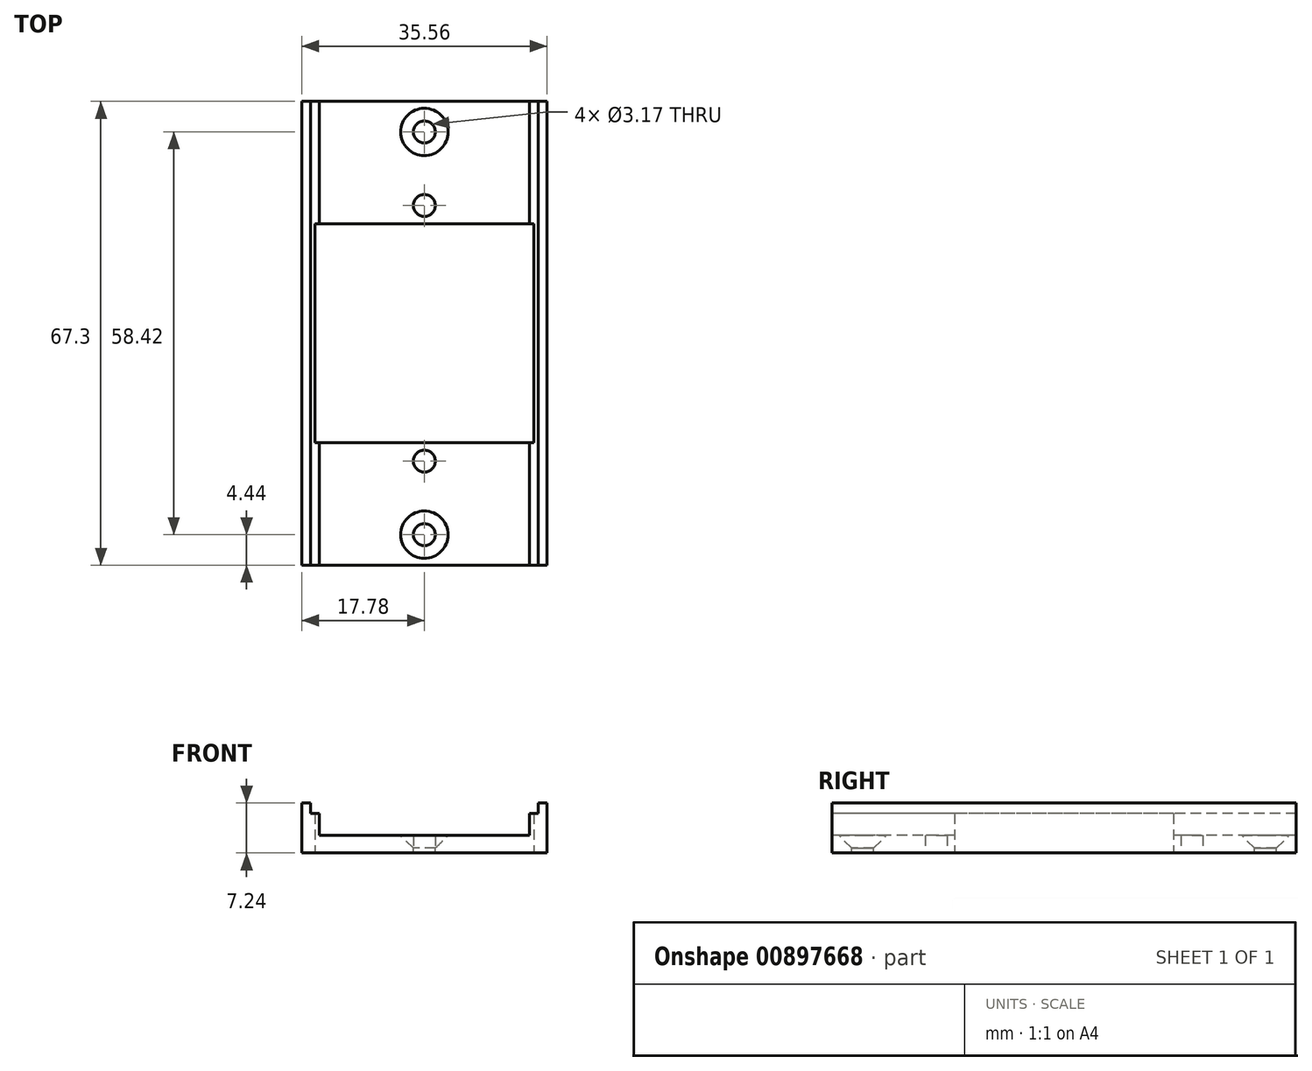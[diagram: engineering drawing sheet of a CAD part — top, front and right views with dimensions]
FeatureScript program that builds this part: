
annotation { "Feature Type Name" : "Feature", "Feature Type Description" : "" }
export const myFeature = defineFeature(function(context is Context, id is Id, definition is map)
    precondition{}
    {
        {
            var Q0;
            Q0=qCreatedBy(makeId("Top.planeOp"),FACE);
            var sketch = newSketch(context, id + "F0", { "sketchPlane" : qUnion([Q0])});
            skLineSegment(sketch, "E0.bottom", {"start": v(17.78, 33.66) * mm, "end": v(-17.78, 33.66) * mm});
            skLineSegment(sketch, "E0.top", {"start": v(17.78, -33.65) * mm, "end": v(-17.78, -33.65) * mm});
            skLineSegment(sketch, "E0.left", {"start": v(17.78, 33.66) * mm, "end": v(17.78, -33.65) * mm});
            skLineSegment(sketch, "E0.right", {"start": v(-17.78, 33.66) * mm, "end": v(-17.78, -33.65) * mm});
            skPoint(sketch, "E1", {"position": v(0, 18.54) * mm});
            skPoint(sketch, "E2", {"position": v(0, -18.54) * mm});
            skLineSegment(sketch, "E3.bottom", {"start": v(15.88, 15.88) * mm, "end": v(-15.88, 15.88) * mm});
            skLineSegment(sketch, "E3.top", {"start": v(15.88, -15.88) * mm, "end": v(-15.88, -15.88) * mm});
            skLineSegment(sketch, "E3.left", {"start": v(15.88, 15.88) * mm, "end": v(15.88, -15.88) * mm});
            skLineSegment(sketch, "E3.right", {"start": v(-15.88, 15.88) * mm, "end": v(-15.88, -15.88) * mm});
            skPoint(sketch, "E3.middle", {"position": v(0, 0) * mm});
            skSolve(sketch);
        }
        {
            var Q0;
            Q0=makeQuery(id+"F0.imprint","IMPRINT",FACE,{"disambiguationData":[TD([[makeQuery(id+"F0.imprint","IMPRINT",EDGE,{"derivedFrom":sQuery(id+"F0.wireOp",EDGE,"E0.bottom")}),1.0]])]});
            extrude(context, id + "F1", {"entities" : qUnion([Q0]), "depth" : 2.54 * mm, "offsetDistance" : 25.4 * mm});
        }
        {
            var Q0;
            Q0=makeQuery(id+"F1.opExtrude","CAP_FACE",FACE,{"disambiguationData":[OSD([sQuery(id+"F0.wireOp",EDGE,"E0.bottom"),sQuery(id+"F0.wireOp",EDGE,"E0.top"),sQuery(id+"F0.wireOp",EDGE,"E0.left"),sQuery(id+"F0.wireOp",EDGE,"E0.right"),sQuery(id+"F0.wireOp",EDGE,"5571z992-hKs1-y02k-7Obe-XOOpmXcP6RWi"),sQuery(id+"F0.wireOp",EDGE,"wQNrnPLk-SSpg-0H65-J1RA-0MrzZ9B65Bsl"),sQuery(id+"F0.wireOp",EDGE,"UYcWB7f3-ynK9-RhDb-2wGZ-q95VmTANQqJL"),sQuery(id+"F0.wireOp",EDGE,"Jd4PUpz0-ZYMC-tZpY-tJWR-cS3pFTbUJsl5"),sQuery(id+"F0.wireOp",EDGE,"NS50ZrWx-p5hV-kl1R-m6l1-CCq5c4hJaWFx.bottom"),sQuery(id+"F0.wireOp",EDGE,"NS50ZrWx-p5hV-kl1R-m6l1-CCq5c4hJaWFx.top"),sQuery(id+"F0.wireOp",EDGE,"NS50ZrWx-p5hV-kl1R-m6l1-CCq5c4hJaWFx.left"),sQuery(id+"F0.wireOp",EDGE,"NS50ZrWx-p5hV-kl1R-m6l1-CCq5c4hJaWFx.right")])],"isStart":false});
            var sketch = newSketch(context, id + "F2", { "sketchPlane" : qUnion([Q0])});
            skPoint(sketch, "E4", {"position": v(0, 29.21) * mm});
            skPoint(sketch, "E5", {"position": v(0, -29.2) * mm});
            skSolve(sketch);
        }
        {
            var Q0;
            Q0=sQuery(id+"F2.wireOp",VERTEX,"E4");
            var Q1;
            Q1=sQuery(id+"F2.wireOp",VERTEX,"E5");
            var Q2;
            Q2=makeQuery(id+"F1.opExtrude","SWEPT_BODY",BODY,{"disambiguationData":[OSD([sQuery(id+"F0.wireOp",EDGE,"E0.bottom"),sQuery(id+"F0.wireOp",EDGE,"E0.top"),sQuery(id+"F0.wireOp",EDGE,"E0.left"),sQuery(id+"F0.wireOp",EDGE,"E0.right"),sQuery(id+"F0.wireOp",EDGE,"5571z992-hKs1-y02k-7Obe-XOOpmXcP6RWi"),sQuery(id+"F0.wireOp",EDGE,"wQNrnPLk-SSpg-0H65-J1RA-0MrzZ9B65Bsl"),sQuery(id+"F0.wireOp",EDGE,"UYcWB7f3-ynK9-RhDb-2wGZ-q95VmTANQqJL"),sQuery(id+"F0.wireOp",EDGE,"Jd4PUpz0-ZYMC-tZpY-tJWR-cS3pFTbUJsl5"),sQuery(id+"F0.wireOp",EDGE,"NS50ZrWx-p5hV-kl1R-m6l1-CCq5c4hJaWFx.bottom"),sQuery(id+"F0.wireOp",EDGE,"NS50ZrWx-p5hV-kl1R-m6l1-CCq5c4hJaWFx.top"),sQuery(id+"F0.wireOp",EDGE,"NS50ZrWx-p5hV-kl1R-m6l1-CCq5c4hJaWFx.left"),sQuery(id+"F0.wireOp",EDGE,"NS50ZrWx-p5hV-kl1R-m6l1-CCq5c4hJaWFx.right")])]});
            hole(context, id + "F3", {"style" : HoleStyle.C_SINK, "endStyle" : HoleEndStyle.THROUGH, "holeDiameter" : 3.17 * mm, "cSinkDiameter" : 6.86 * mm, "cSinkAngle" : 90 * degree, "majorDiameter" : 6.35 * mm, "isTappedThrough" : true, "tappedDepth" : 12.7 * mm, "tapClearance" : 3, "locations" : qUnion([Q0, Q1]), "scope" : qUnion([Q2])});
        }
        {
            var Q0;
            Q0=sQuery(id+"F0.wireOp",VERTEX,"E1");
            var Q1;
            Q1=sQuery(id+"F0.wireOp",VERTEX,"E2");
            var Q2;
            Q2=makeQuery(id+"F1.opExtrude","SWEPT_BODY",BODY,{"disambiguationData":[OSD([sQuery(id+"F0.wireOp",EDGE,"E0.bottom"),sQuery(id+"F0.wireOp",EDGE,"E0.top"),sQuery(id+"F0.wireOp",EDGE,"E0.left"),sQuery(id+"F0.wireOp",EDGE,"E0.right"),sQuery(id+"F0.wireOp",EDGE,"5571z992-hKs1-y02k-7Obe-XOOpmXcP6RWi"),sQuery(id+"F0.wireOp",EDGE,"wQNrnPLk-SSpg-0H65-J1RA-0MrzZ9B65Bsl"),sQuery(id+"F0.wireOp",EDGE,"UYcWB7f3-ynK9-RhDb-2wGZ-q95VmTANQqJL"),sQuery(id+"F0.wireOp",EDGE,"Jd4PUpz0-ZYMC-tZpY-tJWR-cS3pFTbUJsl5")])]});
            hole(context, id + "F4", {"style" : HoleStyle.SIMPLE, "endStyle" : HoleEndStyle.THROUGH, "oppositeDirection" : true, "holeDiameter" : 3.17 * mm, "majorDiameter" : 6.35 * mm, "isTappedThrough" : true, "tappedDepth" : 12.7 * mm, "tapClearance" : 3, "locations" : qUnion([Q0, Q1]), "scope" : qUnion([Q2])});
        }
        {
            var Q0;
            Q0=makeQuery(id+"F1.opExtrude","CAP_FACE",FACE,{"disambiguationData":[OSD([sQuery(id+"F0.wireOp",EDGE,"E0.bottom"),sQuery(id+"F0.wireOp",EDGE,"E0.top"),sQuery(id+"F0.wireOp",EDGE,"E0.left"),sQuery(id+"F0.wireOp",EDGE,"E0.right")])],"isStart":false});
            var sketch = newSketch(context, id + "F5", { "sketchPlane" : qUnion([Q0])});
            skLineSegment(sketch, "E6.bottom", {"start": v(-17.78, 33.66) * mm, "end": v(-16.51, 33.66) * mm});
            skLineSegment(sketch, "E6.top", {"start": v(-17.78, -33.65) * mm, "end": v(-16.51, -33.65) * mm});
            skLineSegment(sketch, "E6.left", {"start": v(-17.78, 33.66) * mm, "end": v(-17.78, -33.65) * mm});
            skLineSegment(sketch, "E6.right", {"start": v(-16.51, 33.66) * mm, "end": v(-16.51, -33.65) * mm});
            skLineSegment(sketch, "E7.bottom", {"start": v(17.78, 33.66) * mm, "end": v(16.5, 33.66) * mm});
            skLineSegment(sketch, "E7.top", {"start": v(17.78, -33.65) * mm, "end": v(16.51, -33.65) * mm});
            skLineSegment(sketch, "E7.left", {"start": v(17.78, 33.66) * mm, "end": v(17.78, -33.65) * mm});
            skLineSegment(sketch, "E7.right", {"start": v(16.51, 33.66) * mm, "end": v(16.51, -33.65) * mm});
            skLineSegment(sketch, "E8.bottom", {"start": v(-16.51, 33.66) * mm, "end": v(-15.24, 33.66) * mm});
            skLineSegment(sketch, "E8.top", {"start": v(-16.51, -33.65) * mm, "end": v(-15.24, -33.65) * mm});
            skLineSegment(sketch, "E8.right", {"start": v(-15.24, 33.66) * mm, "end": v(-15.24, -33.65) * mm});
            skLineSegment(sketch, "E9.bottom", {"start": v(16.5, 33.66) * mm, "end": v(15.24, 33.66) * mm});
            skLineSegment(sketch, "E9.top", {"start": v(16.51, -33.65) * mm, "end": v(15.24, -33.65) * mm});
            skLineSegment(sketch, "E9.right", {"start": v(15.24, 33.66) * mm, "end": v(15.24, -33.65) * mm});
            skSolve(sketch);
        }
        {
            var Q0;
            Q0=makeQuery(id+"F5.imprint","IMPRINT",FACE,{"disambiguationData":[TD([[makeQuery(id+"F5.imprint","IMPRINT",EDGE,{"derivedFrom":sQuery(id+"F5.wireOp",EDGE,"E8.bottom")}),1.0]])]});
            var Q1;
            Q1=makeQuery(id+"F5.imprint","IMPRINT",FACE,{"disambiguationData":[TD([[makeQuery(id+"F5.imprint","IMPRINT",EDGE,{"derivedFrom":sQuery(id+"F5.wireOp",EDGE,"E9.bottom")}),1.0]])]});
            extrude(context, id + "F6", {"entities" : qUnion([Q0, Q1]), "operationType" : NewBodyOperationType.ADD, "depth" : 3.17 * mm, "offsetDistance" : 25.4 * mm});
        }
        {
            var Q0;
            {var subQ0=sQuery(id+"F0.wireOp",EDGE,"E0.top");var subQ1=sQuery(id+"F0.wireOp",EDGE,"E0.right");var subQ2=sQuery(id+"F0.wireOp",EDGE,"E0.bottom");Q0=makeQuery(id+"F6.boolean.opBoolean","SPLIT",FACE,{"disambiguationData":[TD([makeQuery(id+"F1.opExtrude","SWEPT_FACE",FACE,{"disambiguationData":[OSD([subQ1])]})])],"derivedFrom":makeQuery(id+"F1.opExtrude","CAP_FACE",FACE,{"disambiguationData":[OSD([subQ2,subQ0,sQuery(id+"F0.wireOp",EDGE,"E0.left"),subQ1])],"isStart":false})});}
            var Q1;
            {var subQ0=sQuery(id+"F0.wireOp",EDGE,"E0.left");var subQ1=sQuery(id+"F0.wireOp",EDGE,"E0.top");var subQ2=sQuery(id+"F0.wireOp",EDGE,"E0.bottom");Q1=makeQuery(id+"F6.boolean.opBoolean","SPLIT",FACE,{"disambiguationData":[TD([makeQuery(id+"F1.opExtrude","SWEPT_FACE",FACE,{"disambiguationData":[OSD([subQ0])]})])],"derivedFrom":makeQuery(id+"F1.opExtrude","CAP_FACE",FACE,{"disambiguationData":[OSD([subQ2,subQ1,subQ0,sQuery(id+"F0.wireOp",EDGE,"E0.right")])],"isStart":false})});}
            extrude(context, id + "F7", {"entities" : qUnion([Q0, Q1]), "operationType" : NewBodyOperationType.ADD, "depth" : 4.7 * mm, "offsetDistance" : 25.4 * mm});
        }
    });
